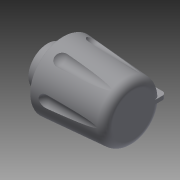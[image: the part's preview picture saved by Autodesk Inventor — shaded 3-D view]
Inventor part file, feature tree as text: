
AUTODESK INVENTOR PART (.ipt)
format: ipt  version: 2016 (Build 200138000, 138)  size: 231,936 bytes
history: native  units: mm
features: fillet x4, sketch x4, extrude x3, revolve x1, pattern_circular x1
ambient origin geometry x8: Origin, YZ Plane, XZ Plane, XY Plane, X Axis, Y Axis, Z Axis, Center Point
bodies: Solid1 (feature_tree)
feature tree (13):
  revolve  "Revolution1"  [1 undecoded]
  extrude  "Extrusion1"  Depth=3.5mm
  extrude  "Extrusion2"  Depth=9.0mm TaperAngle=0.0deg
  fillet  "Fillet1"  Radius=2.5mm
  fillet  "Fillet2"  Radius=2.0mm
  fillet  "Fillet4"  Radius=0.698132mm
  extrude  "Extrusion3"  Depth=1.0mm
  fillet  "Fillet5"  Radius=1.0mm
  pattern_circular  "Circular Pattern1"  [2 undecoded]
  sketch  "Sketch1"  dims[d0=11.0mm d1=4.4mm]
  sketch  "Sketch2"  dims[d3=90.0deg d4=3.5mm]
  sketch  "Sketch3"  dims[d5=2.5mm d6=9.0mm d7=0.0mm d8=2.5mm d9=2.0mm d10=0.698132mm]
  sketch  "Sketch4"  dims[d11=0.0mm d12=0.25mm d13=1.0mm d14=0.5mm d16=2.0mm d17=10.0mm d18=0.0mm d20=0.0mm d21=0.5mm d22=2.0mm d23=8.0mm d24=0.0mm d25=1.0mm d26=60.0mm d27=360.0deg]
note: 3 required parameter values undecoded (feature->parameter linkage not recoverable at this tier; creation-order binding heuristic only, values carry confidence <= 0.55)